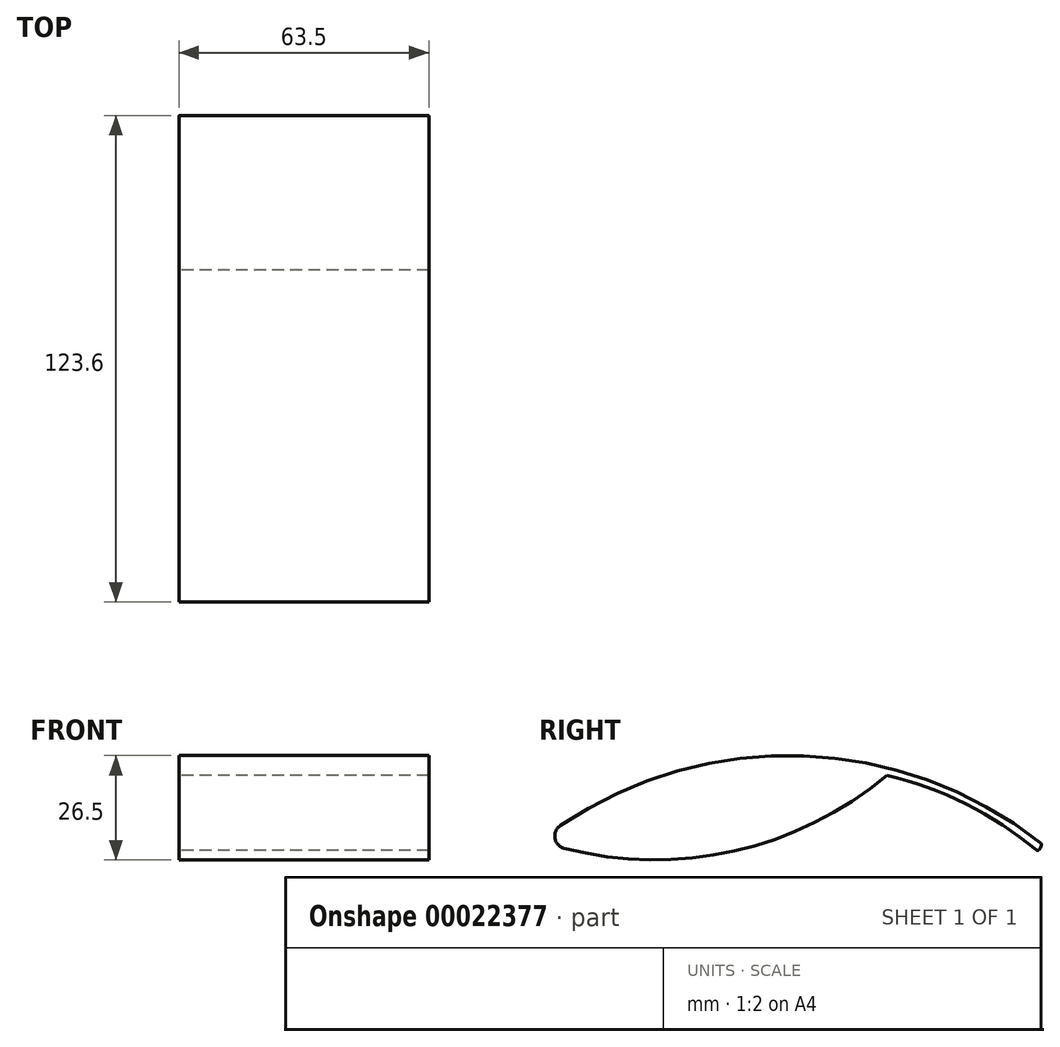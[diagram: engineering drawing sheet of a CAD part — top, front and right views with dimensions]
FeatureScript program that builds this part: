
annotation { "Feature Type Name" : "Feature", "Feature Type Description" : "" }
export const myFeature = defineFeature(function(context is Context, id is Id, definition is map)
    precondition{}
    {
        {
            var Q0;
            Q0=qCreatedBy(makeId("Right.planeOp"),FACE);
            var sketch = newSketch(context, id + "F0", { "sketchPlane" : qUnion([Q0])});
            skArc(sketch, "E0", {"start": v(67.23, -6.55) * mm, "mid": v(6.94, 15.6) * mm, "end": v(-54.79, -2.13) * mm});
            skArc(sketch, "E1", {"start": v(-53.8, -7.88) * mm, "mid": v(-9.43, -8.32) * mm, "end": v(29.94, 12.15) * mm});
            skPoint(sketch, "E2.visualSharp", {"position": v(-60.11, -6) * mm});
            skArc(sketch, "E2.filletArc", {"start": v(-54.79, -2.13) * mm, "mid": v(-56.15, -5.32) * mm, "end": v(-53.8, -7.88) * mm});
            skPoint(sketch, "E3.visualSharp", {"position": v(64.6, -14.5) * mm});
            skPoint(sketch, "E4.visualSharp", {"position": v(67.6, -6.85) * mm});
            skArc(sketch, "E5", {"start": v(66.11, -8.33) * mm, "mid": v(48.26, 3.38) * mm, "end": v(28.18, 10.63) * mm});
            skArc(sketch, "E6", {"start": v(66.7, -8.35) * mm, "mid": v(67.23, -7.72) * mm, "end": v(67.4, -6.9) * mm});
            skPoint(sketch, "E7.visualSharp", {"position": v(66.36, -8.54) * mm});
            skArc(sketch, "E7.filletArc", {"start": v(66.11, -8.33) * mm, "mid": v(66.4, -8.44) * mm, "end": v(66.7, -8.35) * mm});
            skPoint(sketch, "E8.visualSharp", {"position": v(67.38, -6.67) * mm});
            skArc(sketch, "E8.filletArc", {"start": v(67.4, -6.9) * mm, "mid": v(67.36, -6.7) * mm, "end": v(67.23, -6.55) * mm});
            skSolve(sketch);
        }
        {
            var Q0;
            Q0 = qSketchRegion(id + "F0", true);
            extrude(context, id + "F1", {"entities" : qUnion([Q0]), "depth" : 63.5 * mm});
        }
    });
